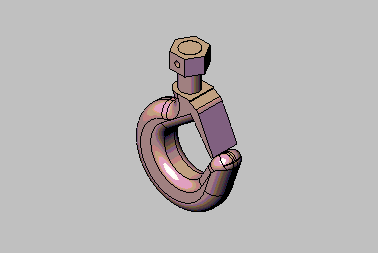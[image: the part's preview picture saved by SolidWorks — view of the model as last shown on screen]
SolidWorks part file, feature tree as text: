
SOLIDWORKS PART (.sldprt)
format: sldprt  version: not decoded by parser v0  size: 1,530,368 bytes
history: native  units: mm
features: plane x5, sketch x4, extrude x3, fillet x2, material x1, mirror x1, cut_extrude x1 (+10 scaffold rows collapsed)
feature tree (27):
  scaffold x10  (default folders/planes/origin — collapsed)
  material  "Material <not specified>"
  plane  "Plane1"  Offset=0mm
  plane  "Plane2"  Offset=0mm
  plane  "Plane3"  Offset=0mm
  sketch  "Sketch1"
  extrude  "Extrude1"  Depth=11.1125mm
  fillet  "Fillet1"  Radius=9.525mm
  fillet  "Fillet2"  Radius=6.35mm
  mirror  "Mirror1"
  sketch  "Sketch2"  dims[D1=15.875mm]
  extrude  "Extrude2"  Depth=31.75mm
  plane  "Plane4"  Offset=0mm
  plane  "Plane5"  Offset=17.4625mm
  sketch  "Sketch3"  dims[D1=23.8125mm]
  extrude  "Extrude3"  Depth=14.1986mm
  sketch  "Sketch4"  dims[D1=4.7625mm D2=7.0866mm]
  cut_extrude  "Cut-Extrude1"  [1 undecoded]
decode coverage: 8 of 11 modeling features carry decoded parameters
note: 1 parameter value undecoded
note: suppression state not decoded; provenance and decode notes live in map.json
